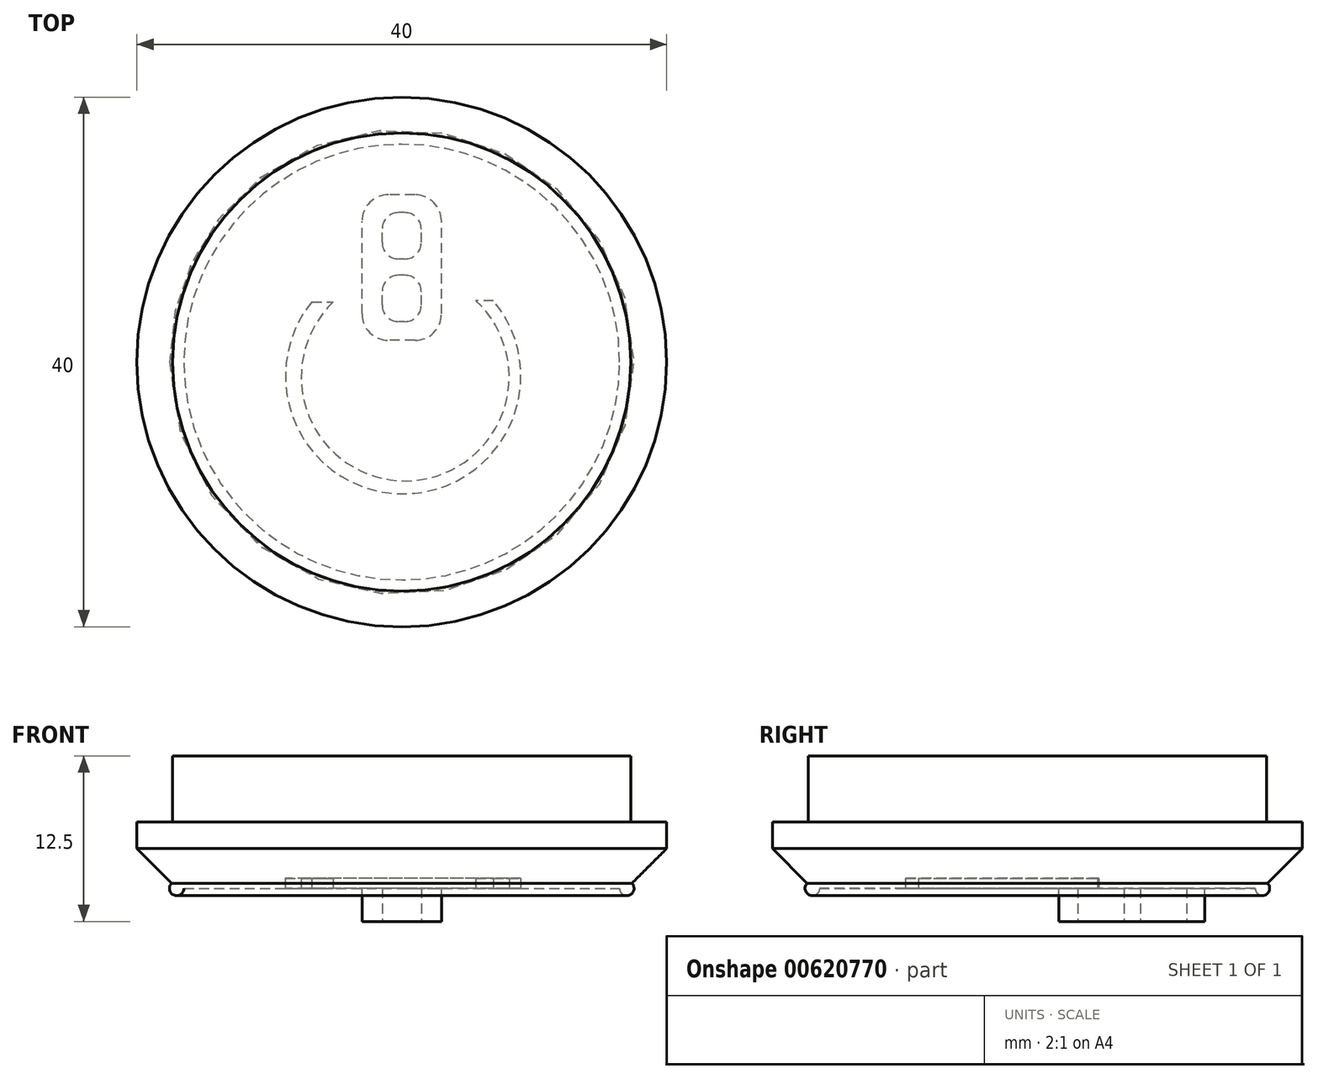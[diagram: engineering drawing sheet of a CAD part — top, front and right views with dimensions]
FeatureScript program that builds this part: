
annotation { "Feature Type Name" : "Feature", "Feature Type Description" : "" }
export const myFeature = defineFeature(function(context is Context, id is Id, definition is map)
    precondition{}
    {
        {
            var Q0;
            Q0=qCreatedBy(makeId("Top.planeOp"),FACE);
            var sketch = newSketch(context, id + "F0", { "sketchPlane" : qUnion([Q0])});
            skCircle(sketch, "E0", {"center": v(0, 0) * mm, "radius": 20 * mm});
            skSolve(sketch);
        }
        {
            var Q0;
            Q0=makeQuery(id+"F0.imprint","IMPRINT",FACE,{"disambiguationData":[TD([[makeQuery(id+"F0.imprint","IMPRINT",EDGE,{"derivedFrom":sQuery(id+"F0.wireOp",EDGE,"E0")}),1.0]])]});
            extrude(context, id + "F1", {"entities" : qUnion([Q0]), "depth" : 5 * mm, "offsetDistance" : 25 * mm});
        }
        {
            var Q0;
            Q0=makeQuery(id+"F1.opExtrude","CAP_FACE",FACE,{"disambiguationData":[OSD([sQuery(id+"F0.wireOp",EDGE,"E0")])],"isStart":false});
            var sketch = newSketch(context, id + "F2", { "sketchPlane" : qUnion([Q0])});
            skCircle(sketch, "E1", {"center": v(0, 0) * mm, "radius": 16.6 * mm});
            skSolve(sketch);
        }
        {
            var Q0;
            Q0=makeQuery(id+"F2.imprint","IMPRINT",FACE,{"disambiguationData":[TD([[makeQuery(id+"F2.imprint","IMPRINT",EDGE,{"derivedFrom":sQuery(id+"F2.wireOp",EDGE,"E1")}),1.0]])]});
            extrude(context, id + "F3", {"entities" : qUnion([Q0]), "operationType" : NewBodyOperationType.ADD, "depth" : 5 * mm, "offsetDistance" : 25 * mm});
        }
        {
            var Q0;
            Q0=makeQuery(id+"F1.opExtrude","CAP_FACE",FACE,{"disambiguationData":[OSD([sQuery(id+"F0.wireOp",EDGE,"E0")])],"isStart":true});
            var sketch = newSketch(context, id + "F4", { "sketchPlane" : qUnion([Q0])});
            skLineSegment(sketch, "E2.bottom", {"start": v(3, -1.64) * mm, "end": v(-3, -1.64) * mm});
            skLineSegment(sketch, "E2.top", {"start": v(3, -12.64) * mm, "end": v(-3, -12.64) * mm});
            skLineSegment(sketch, "E2.left", {"start": v(3, -1.64) * mm, "end": v(3, -12.64) * mm});
            skLineSegment(sketch, "E2.right", {"start": v(-3, -1.64) * mm, "end": v(-3, -12.64) * mm});
            skPoint(sketch, "E2.middle", {"position": v(0, -7.14) * mm});
            skSolve(sketch);
        }
        {
            var Q0;
            Q0 = qSketchRegion(id + "F4", true);
            extrude(context, id + "F5", {"entities" : qUnion([Q0]), "operationType" : NewBodyOperationType.ADD, "depth" : 2.5 * mm, "offsetDistance" : 25 * mm});
        }
        {
            var Q0;
            Q0=makeQuery(id+"F5.opExtrude","SWEPT_EDGE",EDGE,{"disambiguationData":[OSD([sQuery(id+"F4.wireOp",EDGE,"E2.top"),sQuery(id+"F4.wireOp",EDGE,"E2.right")])]});
            var Q1;
            Q1=makeQuery(id+"F5.opExtrude","SWEPT_EDGE",EDGE,{"disambiguationData":[OSD([sQuery(id+"F4.wireOp",EDGE,"E2.top"),sQuery(id+"F4.wireOp",EDGE,"E2.left")])]});
            var Q2;
            Q2=makeQuery(id+"F5.opExtrude","SWEPT_EDGE",EDGE,{"disambiguationData":[OSD([sQuery(id+"F4.wireOp",EDGE,"E2.bottom"),sQuery(id+"F4.wireOp",EDGE,"E2.left")])]});
            var Q3;
            Q3=makeQuery(id+"F5.opExtrude","SWEPT_EDGE",EDGE,{"disambiguationData":[OSD([sQuery(id+"F4.wireOp",EDGE,"E2.bottom"),sQuery(id+"F4.wireOp",EDGE,"E2.right")])]});
            fillet(context, id + "F6", {"entities" : qUnion([Q0, Q1, Q2, Q3]), "radius" : 2 * mm, "tangentPropagation" : true, "allowEdgeOverflow" : false});
        }
        {
            var Q0;
            Q0=makeQuery(id+"F1.opExtrude","CAP_EDGE",EDGE,{"disambiguationData":[OSD([sQuery(id+"F0.wireOp",EDGE,"E0")])],"isStart":true});
            chamfer(context, id + "F7", {"entities" : qUnion([Q0]), "width" : 3 * mm, "tangentPropagation" : true});
        }
        {
            var Q0;
            Q0=makeQuery(id+"F5.opExtrude","CAP_FACE",FACE,{"disambiguationData":[OSD([sQuery(id+"F4.wireOp",EDGE,"E2.bottom"),sQuery(id+"F4.wireOp",EDGE,"E2.top"),sQuery(id+"F4.wireOp",EDGE,"E2.left"),sQuery(id+"F4.wireOp",EDGE,"E2.right")])],"isStart":false});
            var sketch = newSketch(context, id + "F8", { "sketchPlane" : qUnion([Q0])});
            skLineSegment(sketch, "E3.bottom", {"start": v(1.48, -7.79) * mm, "end": v(-1.48, -7.79) * mm});
            skLineSegment(sketch, "E3.top", {"start": v(1.48, -11.29) * mm, "end": v(-1.48, -11.29) * mm});
            skLineSegment(sketch, "E3.left", {"start": v(1.48, -7.79) * mm, "end": v(1.48, -11.29) * mm});
            skLineSegment(sketch, "E3.right", {"start": v(-1.48, -7.79) * mm, "end": v(-1.48, -11.29) * mm});
            skPoint(sketch, "E3.middle", {"position": v(0, -9.54) * mm});
            skLineSegment(sketch, "E4.bottom", {"start": v(1.48, -3.06) * mm, "end": v(-1.48, -3.06) * mm});
            skLineSegment(sketch, "E4.top", {"start": v(1.48, -6.56) * mm, "end": v(-1.48, -6.56) * mm});
            skLineSegment(sketch, "E4.left", {"start": v(1.48, -3.06) * mm, "end": v(1.48, -6.56) * mm});
            skLineSegment(sketch, "E4.right", {"start": v(-1.48, -3.06) * mm, "end": v(-1.48, -6.56) * mm});
            skPoint(sketch, "E4.middle", {"position": v(0, -4.8) * mm});
            skSolve(sketch);
        }
        {
            var Q0;
            Q0=makeQuery(id+"F8.imprint","IMPRINT",FACE,{"disambiguationData":[TD([[makeQuery(id+"F8.imprint","IMPRINT",EDGE,{"derivedFrom":sQuery(id+"F8.wireOp",EDGE,"E4.bottom")}),1.0]])]});
            var Q1;
            Q1=makeQuery(id+"F8.imprint","IMPRINT",FACE,{"disambiguationData":[TD([[makeQuery(id+"F8.imprint","IMPRINT",EDGE,{"derivedFrom":sQuery(id+"F8.wireOp",EDGE,"E3.bottom")}),1.0]])]});
            extrude(context, id + "F9", {"entities" : qUnion([Q0, Q1]), "operationType" : NewBodyOperationType.REMOVE, "oppositeDirection" : true, "depth" : 2.5 * mm, "offsetDistance" : 25 * mm});
        }
        {
            var Q0;
            Q0=makeQuery(id+"F9.boolean.opBoolean","COPY",EDGE,{"derivedFrom":makeQuery(id+"F9.opExtrude","SWEPT_EDGE",EDGE,{"disambiguationData":[OSD([sQuery(id+"F8.wireOp",EDGE,"E4.bottom"),sQuery(id+"F8.wireOp",EDGE,"E4.left")])]})});
            var Q1;
            Q1=makeQuery(id+"F9.boolean.opBoolean","COPY",EDGE,{"derivedFrom":makeQuery(id+"F9.opExtrude","SWEPT_EDGE",EDGE,{"disambiguationData":[OSD([sQuery(id+"F8.wireOp",EDGE,"E4.bottom"),sQuery(id+"F8.wireOp",EDGE,"E4.right")])]})});
            var Q2;
            Q2=makeQuery(id+"F9.boolean.opBoolean","COPY",EDGE,{"derivedFrom":makeQuery(id+"F9.opExtrude","SWEPT_EDGE",EDGE,{"disambiguationData":[OSD([sQuery(id+"F8.wireOp",EDGE,"E4.top"),sQuery(id+"F8.wireOp",EDGE,"E4.left")])]})});
            var Q3;
            Q3=makeQuery(id+"F9.boolean.opBoolean","COPY",EDGE,{"derivedFrom":makeQuery(id+"F9.opExtrude","SWEPT_EDGE",EDGE,{"disambiguationData":[OSD([sQuery(id+"F8.wireOp",EDGE,"E4.top"),sQuery(id+"F8.wireOp",EDGE,"E4.right")])]})});
            var Q4;
            Q4=makeQuery(id+"F9.boolean.opBoolean","COPY",EDGE,{"derivedFrom":makeQuery(id+"F9.opExtrude","SWEPT_EDGE",EDGE,{"disambiguationData":[OSD([sQuery(id+"F8.wireOp",EDGE,"E3.bottom"),sQuery(id+"F8.wireOp",EDGE,"E3.left")])]})});
            var Q5;
            Q5=makeQuery(id+"F9.boolean.opBoolean","COPY",EDGE,{"derivedFrom":makeQuery(id+"F9.opExtrude","SWEPT_EDGE",EDGE,{"disambiguationData":[OSD([sQuery(id+"F8.wireOp",EDGE,"E3.bottom"),sQuery(id+"F8.wireOp",EDGE,"E3.right")])]})});
            var Q6;
            Q6=makeQuery(id+"F9.boolean.opBoolean","COPY",EDGE,{"derivedFrom":makeQuery(id+"F9.opExtrude","SWEPT_EDGE",EDGE,{"disambiguationData":[OSD([sQuery(id+"F8.wireOp",EDGE,"E3.top"),sQuery(id+"F8.wireOp",EDGE,"E3.right")])]})});
            var Q7;
            Q7=makeQuery(id+"F9.boolean.opBoolean","COPY",EDGE,{"derivedFrom":makeQuery(id+"F9.opExtrude","SWEPT_EDGE",EDGE,{"disambiguationData":[OSD([sQuery(id+"F8.wireOp",EDGE,"E3.top"),sQuery(id+"F8.wireOp",EDGE,"E3.left")])]})});
            fillet(context, id + "F10", {"entities" : qUnion([Q0, Q1, Q2, Q3, Q4, Q5, Q6, Q7]), "radius" : 1.25 * mm, "tangentPropagation" : true, "allowEdgeOverflow" : false});
        }
        {
            var Q0;
            Q0=makeQuery(id+"F1.opExtrude","CAP_FACE",FACE,{"disambiguationData":[OSD([sQuery(id+"F0.wireOp",EDGE,"E0")])],"isStart":true});
            var sketch = newSketch(context, id + "F11", { "sketchPlane" : qUnion([Q0])});
            skArc(sketch, "E5", {"start": v(6.93, -4.64) * mm, "mid": v(0.17, 9.95) * mm, "end": v(-6.8, -4.54) * mm});
            skArc(sketch, "E6", {"start": v(5.6, -4.64) * mm, "mid": v(0.33, 8.97) * mm, "end": v(-5.17, -4.54) * mm});
            skLineSegment(sketch, "E7", {"start": v(-6.8, -4.54) * mm, "end": v(-5.17, -4.54) * mm});
            skLineSegment(sketch, "E8", {"start": v(6.93, -4.64) * mm, "end": v(5.6, -4.64) * mm});
            skSolve(sketch);
        }
        {
            var Q0;
            Q0 = qSketchRegion(id + "F11", true);
            extrude(context, id + "F12", {"entities" : qUnion([Q0]), "operationType" : NewBodyOperationType.REMOVE, "oppositeDirection" : true, "depth" : .75 * mm, "offsetDistance" : 25 * mm});
        }
        {
            var Q0;
            Q0=qCreatedBy(makeId("Right.planeOp"),FACE);
            var sketch = newSketch(context, id + "F13", { "sketchPlane" : qUnion([Q0])});
            skCircle(sketch, "E9", {"center": v(-17, 0) * mm, "radius": 0.55 * mm});
            skLineSegment(sketch, "E10", {"start": v(0, 0) * mm, "end": v(0, -5.19) * mm});
            skSolve(sketch);
        }
        {
            var Q0;
            Q0 = qSketchRegion(id + "F13", true);
            var Q1;
            Q1=sQuery(id+"F13.wireOp",EDGE,"E10");
            revolve(context, id + "F14", {"operationType" : NewBodyOperationType.ADD, "entities" : qUnion([Q0]), "axis" : qUnion([Q1]), "revolveType" : RevolveType.FULL});
        }
        {
            var Q0;
            Q0=makeQuery(id+"F3.opExtrude","CAP_FACE",FACE,{"disambiguationData":[OSD([sQuery(id+"F2.wireOp",EDGE,"E1")])],"isStart":false});
            var sketch = newSketch(context, id + "F15", { "sketchPlane" : qUnion([Q0])});
            skCircle(sketch, "E11", {"center": v(0, 0) * mm, "radius": 17.3 * mm});
            skSolve(sketch);
        }
        {
            var Q0;
            Q0=makeQuery(id+"F15.imprint","IMPRINT",FACE,{"disambiguationData":[TD([[makeQuery(id+"F15.imprint","IMPRINT",EDGE,{"derivedFrom":sQuery(id+"F15.wireOp",EDGE,"E11")}),1.0]])]});
            extrude(context, id + "F16", {"entities" : qUnion([Q0]), "operationType" : NewBodyOperationType.ADD, "oppositeDirection" : true, "depth" : 5 * mm, "offsetDistance" : 25 * mm});
        }
    });
